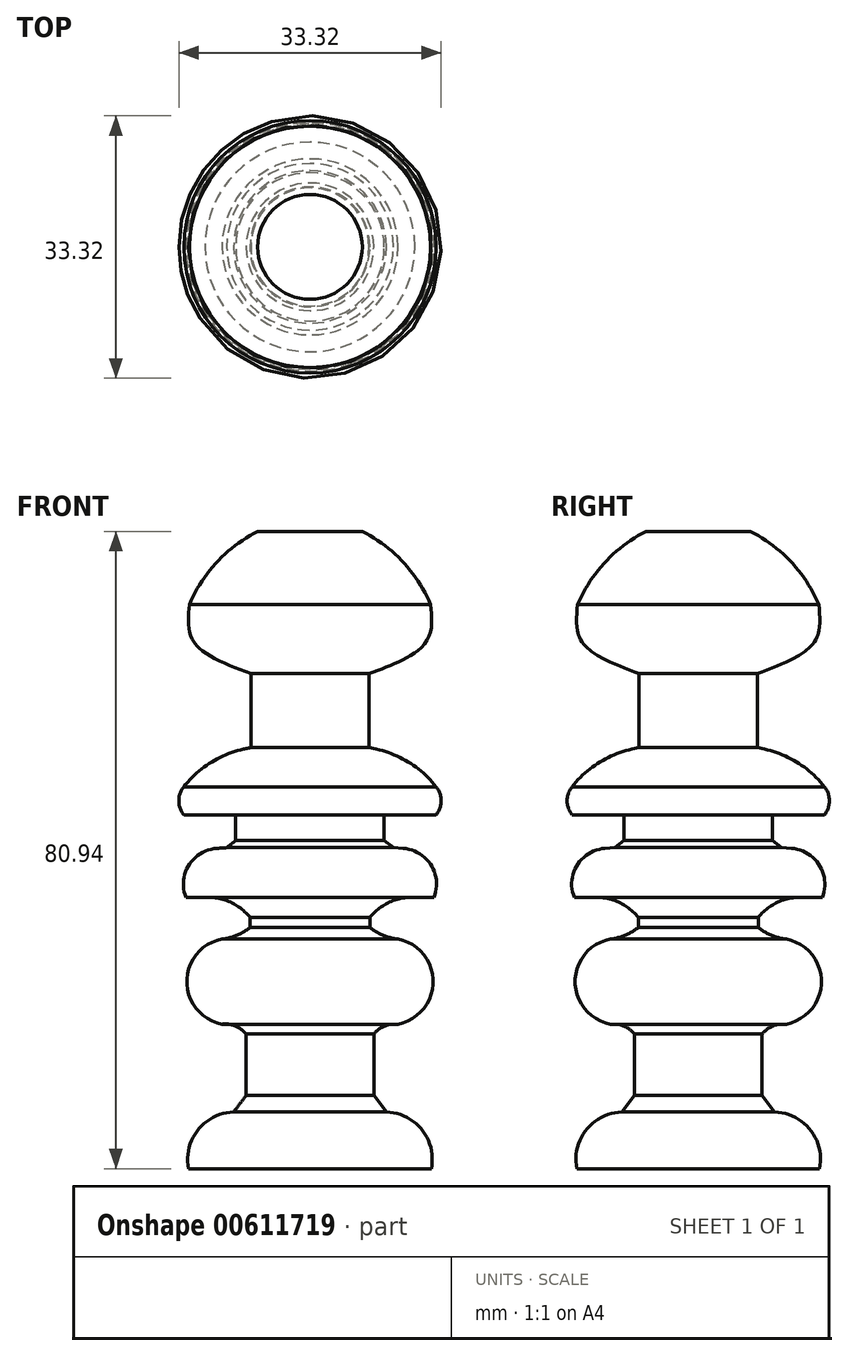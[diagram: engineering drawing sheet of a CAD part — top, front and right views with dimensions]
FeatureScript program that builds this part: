
annotation { "Feature Type Name" : "Feature", "Feature Type Description" : "" }
export const myFeature = defineFeature(function(context is Context, id is Id, definition is map)
    precondition{}
    {
        {
            var Q0;
            Q0=qCreatedBy(makeId("Front.planeOp"),FACE);
            var sketch = newSketch(context, id + "F0", { "sketchPlane" : qUnion([Q0])});
            skLineSegment(sketch, "E0", {"start": v(0, -29.17) * mm, "end": v(-15.4, -29.17) * mm});
            skArc(sketch, "E1", {"start": v(-9.7, -21.98) * mm, "mid": v(-14.23, -24.24) * mm, "end": v(-15.4, -29.17) * mm});
            skLineSegment(sketch, "E2", {"start": v(-9.7, -21.98) * mm, "end": v(-8.1, -19.86) * mm});
            skLineSegment(sketch, "E3", {"start": v(-8.1, -19.86) * mm, "end": v(-8.1, -12.08) * mm});
            skArc(sketch, "E4", {"start": v(-8.1, -12.08) * mm, "mid": v(-9.48, -11.05) * mm, "end": v(-11.17, -10.81) * mm});
            skArc(sketch, "E5", {"start": v(-11.17, 0) * mm, "mid": v(-15.64, -5.4) * mm, "end": v(-11.17, -10.81) * mm});
            skArc(sketch, "E6", {"start": v(-11.17, 0) * mm, "mid": v(-9.28, 0.48) * mm, "end": v(-7.61, 1.48) * mm});
            skLineSegment(sketch, "E7", {"start": v(-7.61, 1.48) * mm, "end": v(-7.61, 2.73) * mm});
            skArc(sketch, "E8", {"start": v(-7.61, 2.73) * mm, "mid": v(-10.15, 4.71) * mm, "end": v(-13.32, 5.29) * mm});
            skLineSegment(sketch, "E9", {"start": v(-13.32, 5.29) * mm, "end": v(-15.75, 5.29) * mm});
            skArc(sketch, "E10", {"start": v(-11.84, 11.52) * mm, "mid": v(-15.38, 9.4) * mm, "end": v(-15.75, 5.29) * mm});
            skLineSegment(sketch, "E11", {"start": v(-11.84, 11.52) * mm, "end": v(-10.58, 11.6) * mm});
            skLineSegment(sketch, "E12", {"start": v(-10.58, 11.6) * mm, "end": v(-9.43, 12.52) * mm});
            skLineSegment(sketch, "E13", {"start": v(-9.43, 12.52) * mm, "end": v(-9.43, 15.78) * mm});
            skLineSegment(sketch, "E14", {"start": v(-9.43, 15.78) * mm, "end": v(-16.02, 15.78) * mm});
            skArc(sketch, "E15", {"start": v(-16.02, 19.35) * mm, "mid": v(-16.66, 17.56) * mm, "end": v(-16.02, 15.78) * mm});
            skArc(sketch, "E16", {"start": v(-8.42, 24.13) * mm, "mid": v(-12.64, 22.4) * mm, "end": v(-16.02, 19.35) * mm});
            skLineSegment(sketch, "E17", {"start": v(-8.42, 24.13) * mm, "end": v(-7.5, 24.33) * mm});
            skLineSegment(sketch, "E18", {"start": v(-7.5, 24.33) * mm, "end": v(-7.5, 33.72) * mm});
            skFitSpline(sketch, "E19", {"points": [v(-7.5, 33.72) * mm, v(-14.76, 37.74) * mm, v(-15.32, 42.48) * mm], "startDerivative": vector(-16.01, 5.95) * mm, "endDerivative": vector(1.17, 11.83) * mm});
            skArc(sketch, "E20", {"start": v(-6.65, 51.77) * mm, "mid": v(-11.81, 47.9) * mm, "end": v(-15.32, 42.48) * mm});
            skLineSegment(sketch, "E21", {"start": v(-6.65, 51.77) * mm, "end": v(0, 51.77) * mm});
            skLineSegment(sketch, "E22", {"start": v(0, 51.77) * mm, "end": v(0, -29.17) * mm});
            skSolve(sketch);
        }
        {
            var Q0;
            Q0 = qSketchRegion(id + "F0", true);
            var Q1;
            Q1=sQuery(id+"F0.wireOp",EDGE,"E21");
            var Q2;
            Q2=sQuery(id+"F0.wireOp",EDGE,"E20");
            var Q3;
            Q3=sQuery(id+"F0.wireOp",EDGE,"E19");
            var Q4;
            Q4=sQuery(id+"F0.wireOp",EDGE,"E18");
            var Q5;
            Q5=sQuery(id+"F0.wireOp",EDGE,"E16");
            var Q6;
            Q6=sQuery(id+"F0.wireOp",EDGE,"E17");
            var Q7;
            Q7=sQuery(id+"F0.wireOp",EDGE,"E15");
            var Q8;
            Q8=sQuery(id+"F0.wireOp",EDGE,"E14");
            var Q9;
            Q9=sQuery(id+"F0.wireOp",EDGE,"E13");
            var Q10;
            Q10=sQuery(id+"F0.wireOp",EDGE,"E12");
            var Q11;
            Q11=sQuery(id+"F0.wireOp",EDGE,"E11");
            var Q12;
            Q12=sQuery(id+"F0.wireOp",EDGE,"E10");
            var Q13;
            Q13=sQuery(id+"F0.wireOp",EDGE,"E9");
            var Q14;
            Q14=sQuery(id+"F0.wireOp",EDGE,"E8");
            var Q15;
            Q15=sQuery(id+"F0.wireOp",EDGE,"E7");
            var Q16;
            Q16=sQuery(id+"F0.wireOp",EDGE,"E6");
            var Q17;
            Q17=sQuery(id+"F0.wireOp",EDGE,"E5");
            var Q18;
            Q18=sQuery(id+"F0.wireOp",EDGE,"E4");
            var Q19;
            Q19=sQuery(id+"F0.wireOp",EDGE,"E3");
            var Q20;
            Q20=sQuery(id+"F0.wireOp",EDGE,"E2");
            var Q21;
            Q21=sQuery(id+"F0.wireOp",EDGE,"E1");
            var Q22;
            Q22=sQuery(id+"F0.wireOp",EDGE,"E0");
            var Q23;
            Q23=sQuery(id+"F0.wireOp",EDGE,"E22");
            revolve(context, id + "F1", {"bodyType" : ToolBodyType.SURFACE, "entities" : qUnion([Q0]), "surfaceEntities" : qUnion([Q1, Q2, Q3, Q4, Q5, Q6, Q7, Q8, Q9, Q10, Q11, Q12, Q13, Q14, Q15, Q16, Q17, Q18, Q19, Q20, Q21, Q22]), "axis" : qUnion([Q23]), "revolveType" : RevolveType.FULL});
        }
    });
